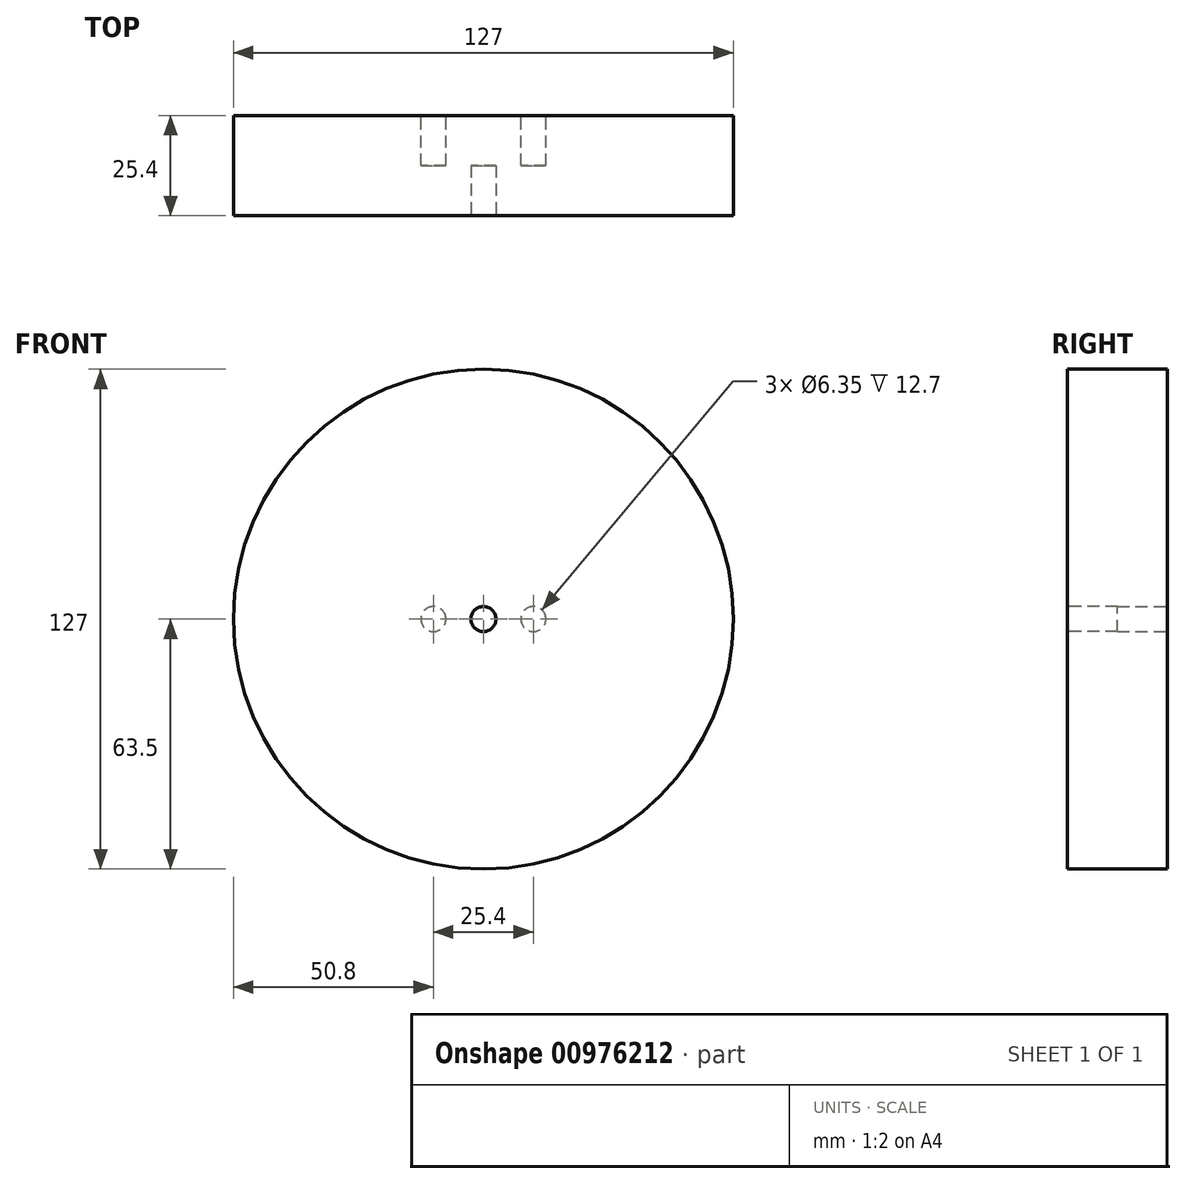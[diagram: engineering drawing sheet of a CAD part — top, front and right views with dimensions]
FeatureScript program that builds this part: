
annotation { "Feature Type Name" : "Feature", "Feature Type Description" : "" }
export const myFeature = defineFeature(function(context is Context, id is Id, definition is map)
    precondition{}
    {
        {
            var Q0;
            Q0=qCreatedBy(makeId("Front.planeOp"),FACE);
            var sketch = newSketch(context, id + "F0", { "sketchPlane" : qUnion([Q0])});
            skCircle(sketch, "E0", {"center": v(0, 0) * mm, "radius": 63.5 * mm});
            skSolve(sketch);
        }
        {
            var Q0;
            Q0 = qSketchRegion(id + "F0", true);
            extrude(context, id + "F1", {"entities" : qUnion([Q0]), "depth" : 25.4 * mm, "offsetDistance" : 25.4 * mm});
        }
        {
            var Q0;
            Q0=makeQuery(id+"F1.opExtrude","CAP_FACE",FACE,{"disambiguationData":[OSD([sQuery(id+"F0.wireOp",EDGE,"E0")])],"isStart":false});
            var sketch = newSketch(context, id + "F2", { "sketchPlane" : qUnion([Q0])});
            skCircle(sketch, "E1", {"center": v(0, 0) * mm, "radius": 3.18 * mm});
            skSolve(sketch);
        }
        {
            var Q0;
            Q0=makeQuery(id+"F1.opExtrude","CAP_FACE",FACE,{"disambiguationData":[OSD([sQuery(id+"F0.wireOp",EDGE,"E0")])],"isStart":false});
            var sketch = newSketch(context, id + "F3", { "sketchPlane" : qUnion([Q0])});
            skSolve(sketch);
        }
        {
            var Q0;
            Q0=makeQuery(id+"F3.imprint","IMPRINT",FACE,{"disambiguationData":[TD([[makeQuery(id+"F3.imprint","IMPRINT",EDGE,{"derivedFrom":makeQuery(id+"F1.opExtrude","CAP_EDGE",EDGE,{"disambiguationData":[OSD([sQuery(id+"F0.wireOp",EDGE,"E0")])],"isStart":false})}),1.0]])]});
            var sketch = newSketch(context, id + "F4", { "sketchPlane" : qUnion([Q0])});
            skCircle(sketch, "E2", {"center": v(0, 0) * mm, "radius": 3.18 * mm});
            skSolve(sketch);
        }
        {
            var Q0;
            Q0 = qSketchRegion(id + "F4", true);
            extrude(context, id + "F5", {"entities" : qUnion([Q0]), "operationType" : NewBodyOperationType.REMOVE, "oppositeDirection" : true, "depth" : 12.7 * mm, "offsetDistance" : 25.4 * mm});
        }
        {
            var Q0;
            Q0=makeQuery(id+"F1.opExtrude","CAP_FACE",FACE,{"disambiguationData":[OSD([sQuery(id+"F0.wireOp",EDGE,"E0")])],"isStart":true});
            var sketch = newSketch(context, id + "F6", { "sketchPlane" : qUnion([Q0])});
            skCircle(sketch, "E3", {"center": v(-12.7, 0) * mm, "radius": 3.18 * mm});
            skCircle(sketch, "E4", {"center": v(12.7, 0) * mm, "radius": 3.18 * mm});
            skSolve(sketch);
        }
        {
            var Q0;
            Q0=makeQuery(id+"F6.imprint","IMPRINT",FACE,{"disambiguationData":[TD([[makeQuery(id+"F6.imprint","IMPRINT",EDGE,{"derivedFrom":sQuery(id+"F6.wireOp",EDGE,"E3")}),1.0]])]});
            var Q1;
            Q1=makeQuery(id+"F6.imprint","IMPRINT",FACE,{"disambiguationData":[TD([[makeQuery(id+"F6.imprint","IMPRINT",EDGE,{"derivedFrom":sQuery(id+"F6.wireOp",EDGE,"E4")}),1.0]])]});
            extrude(context, id + "F7", {"entities" : qUnion([Q0, Q1]), "operationType" : NewBodyOperationType.REMOVE, "oppositeDirection" : true, "depth" : 12.7 * mm, "offsetDistance" : 25.4 * mm});
        }
    });
